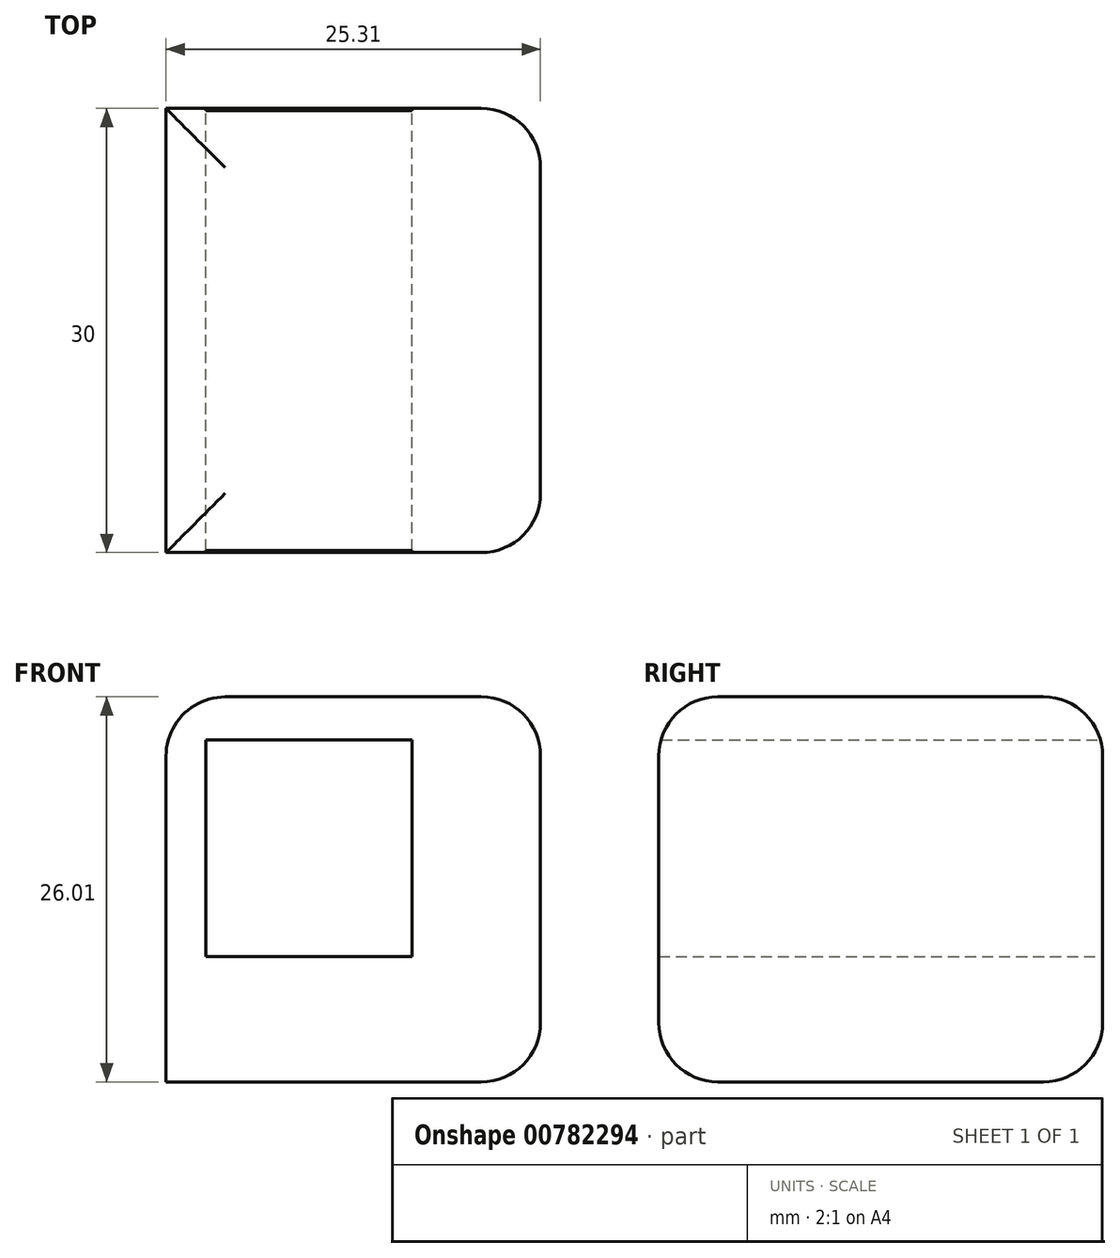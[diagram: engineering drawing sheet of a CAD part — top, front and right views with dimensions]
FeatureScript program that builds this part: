
annotation { "Feature Type Name" : "Feature", "Feature Type Description" : "" }
export const myFeature = defineFeature(function(context is Context, id is Id, definition is map)
    precondition{}
    {
        {
            var Q0;
            Q0=qCreatedBy(makeId("Front.planeOp"),FACE);
            var sketch = newSketch(context, id + "F0", { "sketchPlane" : qUnion([Q0])});
            skLineSegment(sketch, "E0.bottom", {"start": v(0, 0) * mm, "end": v(0, 0) * mm});
            skLineSegment(sketch, "E0.top", {"start": v(0, 0) * mm, "end": v(0, 0) * mm});
            skLineSegment(sketch, "E0.left", {"start": v(0, 0) * mm, "end": v(0, 0) * mm});
            skLineSegment(sketch, "E0.right", {"start": v(0, 0) * mm, "end": v(0, 0) * mm});
            skPoint(sketch, "E0.middle", {"position": v(0, 0) * mm});
            skLineSegment(sketch, "E1.bottom", {"start": v(0, 0) * mm, "end": v(25.31, 0) * mm});
            skLineSegment(sketch, "E1.top", {"start": v(0, 26.01) * mm, "end": v(25.31, 26.01) * mm});
            skLineSegment(sketch, "E1.left", {"start": v(0, 0) * mm, "end": v(0, 26.01) * mm});
            skLineSegment(sketch, "E1.right", {"start": v(25.31, 0) * mm, "end": v(25.31, 26.01) * mm});
            skPoint(sketch, "E1.middle", {"position": v(12.66, 13) * mm});
            skSolve(sketch);
        }
        {
            var Q0;
            Q0=makeQuery(id+"F0.imprint","IMPRINT",FACE,{"disambiguationData":[TD([[makeQuery(id+"F0.imprint","IMPRINT",EDGE,{"derivedFrom":sQuery(id+"F0.wireOp",EDGE,"E1.bottom")}),1.0]])]});
            extrude(context, id + "F1", {"entities" : qUnion([Q0]), "depth" : 30 * mm, "offsetDistance" : 25.4 * mm});
        }
        {
            var Q0;
            Q0=makeQuery(id+"F1.opExtrude","CAP_FACE",FACE,{"disambiguationData":[OSD([sQuery(id+"F0.wireOp",EDGE,"E1.bottom"),sQuery(id+"F0.wireOp",EDGE,"E1.top"),sQuery(id+"F0.wireOp",EDGE,"E1.left"),sQuery(id+"F0.wireOp",EDGE,"E1.right")])],"isStart":true});
            var sketch = newSketch(context, id + "F2", { "sketchPlane" : qUnion([Q0])});
            skLineSegment(sketch, "E2.bottom", {"start": v(-16.63, 8.46) * mm, "end": v(-2.69, 8.46) * mm});
            skLineSegment(sketch, "E2.top", {"start": v(-16.63, 23.1) * mm, "end": v(-2.69, 23.1) * mm});
            skLineSegment(sketch, "E2.left", {"start": v(-16.63, 8.46) * mm, "end": v(-16.63, 23.1) * mm});
            skLineSegment(sketch, "E2.right", {"start": v(-2.69, 8.46) * mm, "end": v(-2.69, 23.1) * mm});
            skSolve(sketch);
        }
        {
            var Q0;
            Q0 = qSketchRegion(id + "F2", true);
            extrude(context, id + "F3", {"entities" : qUnion([Q0]), "operationType" : NewBodyOperationType.REMOVE, "oppositeDirection" : true, "depth" : 32 * mm, "offsetDistance" : 25.4 * mm});
        }
        {
            var Q0;
            Q0=makeQuery(id+"F1.opExtrude","CAP_EDGE",EDGE,{"disambiguationData":[OSD([sQuery(id+"F0.wireOp",EDGE,"E1.right")])],"isStart":false});
            var Q1;
            Q1=makeQuery(id+"F1.opExtrude","CAP_EDGE",EDGE,{"disambiguationData":[OSD([sQuery(id+"F0.wireOp",EDGE,"E1.top")])],"isStart":false});
            var Q2;
            Q2=makeQuery(id+"F1.opExtrude","CAP_EDGE",EDGE,{"disambiguationData":[OSD([sQuery(id+"F0.wireOp",EDGE,"E1.bottom")])],"isStart":false});
            var Q3;
            Q3=makeQuery(id+"F1.opExtrude","SWEPT_EDGE",EDGE,{"disambiguationData":[OSD([sQuery(id+"F0.wireOp",EDGE,"E1.bottom"),sQuery(id+"F0.wireOp",EDGE,"E1.right")])]});
            var Q4;
            Q4=makeQuery(id+"F1.opExtrude","SWEPT_EDGE",EDGE,{"disambiguationData":[OSD([sQuery(id+"F0.wireOp",EDGE,"E1.top"),sQuery(id+"F0.wireOp",EDGE,"E1.right")])]});
            var Q5;
            Q5=makeQuery(id+"F1.opExtrude","CAP_EDGE",EDGE,{"disambiguationData":[OSD([sQuery(id+"F0.wireOp",EDGE,"E1.top")])],"isStart":true});
            var Q6;
            Q6=makeQuery(id+"F1.opExtrude","SWEPT_EDGE",EDGE,{"disambiguationData":[OSD([sQuery(id+"F0.wireOp",EDGE,"E1.top"),sQuery(id+"F0.wireOp",EDGE,"E1.left")])]});
            var Q7;
            Q7=makeQuery(id+"F1.opExtrude","CAP_EDGE",EDGE,{"disambiguationData":[OSD([sQuery(id+"F0.wireOp",EDGE,"E1.right")])],"isStart":true});
            fillet(context, id + "F4", {"entities" : qUnion([Q0, Q1, Q2, Q3, Q4, Q5, Q6, Q7]), "radius" : 4 * mm, "tangentPropagation" : true, "allowEdgeOverflow" : false});
        }
        {
            var Q0;
            Q0=makeQuery(id+"F1.opExtrude","CAP_EDGE",EDGE,{"disambiguationData":[OSD([sQuery(id+"F0.wireOp",EDGE,"E1.bottom")])],"isStart":true});
            fillet(context, id + "F5", {"entities" : qUnion([Q0]), "radius" : 4 * mm, "tangentPropagation" : true, "allowEdgeOverflow" : false});
        }
    });
